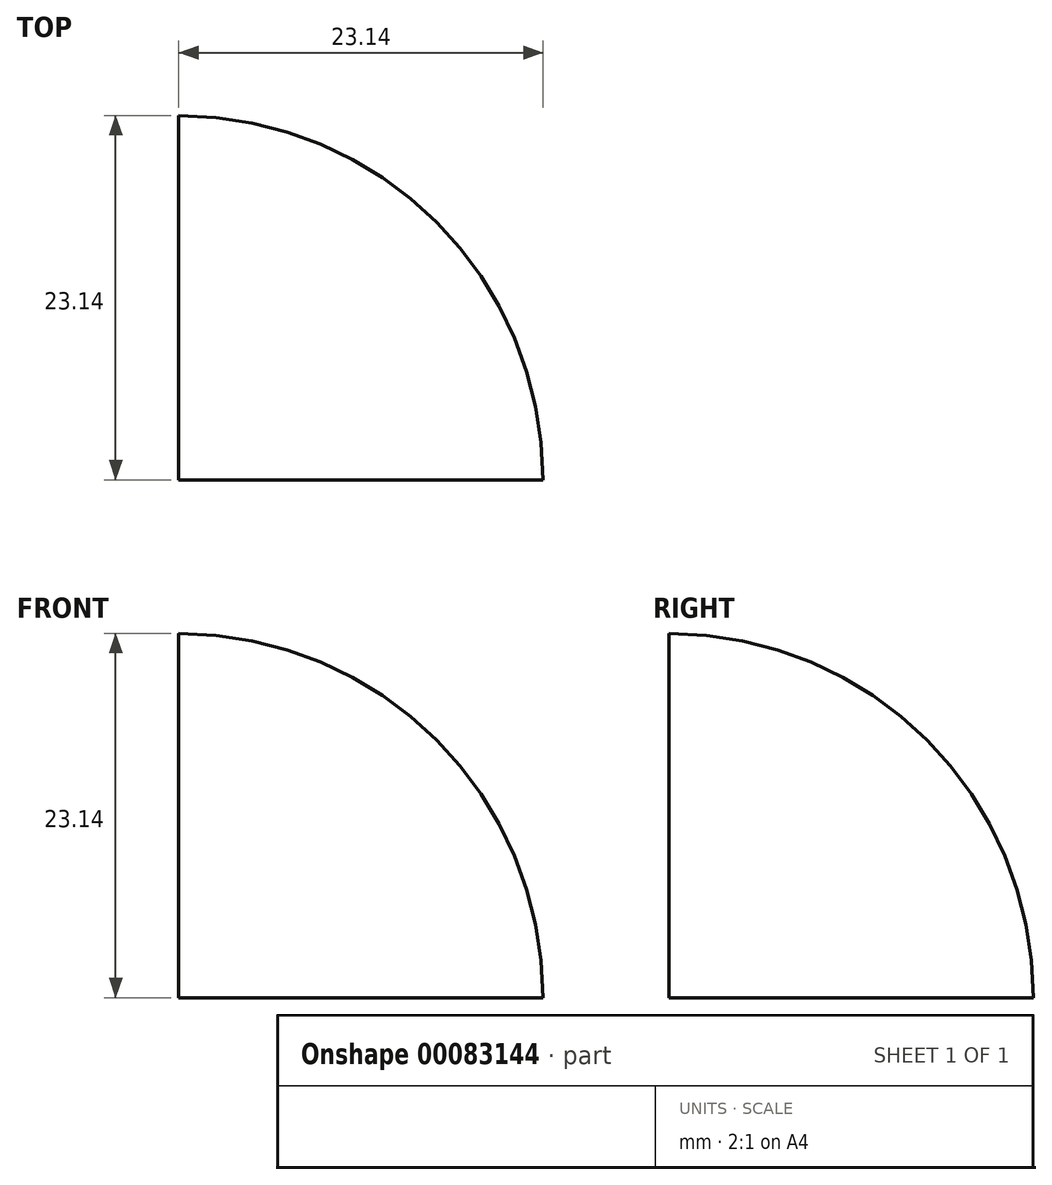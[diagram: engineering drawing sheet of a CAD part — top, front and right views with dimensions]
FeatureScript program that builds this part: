
annotation { "Feature Type Name" : "Feature", "Feature Type Description" : "" }
export const myFeature = defineFeature(function(context is Context, id is Id, definition is map)
    precondition{}
    {
        {
            var Q0;
            Q0=qCreatedBy(makeId("Front.planeOp"),FACE);
            var sketch = newSketch(context, id + "F0", { "sketchPlane" : qUnion([Q0])});
            skPoint(sketch, "E0", {"position": v(0, 0) * mm});
            skPoint(sketch, "E1", {"position": v(35.52, 0) * mm});
            skPoint(sketch, "E2", {"position": v(0, 23.14) * mm});
            skLineSegment(sketch, "E3", {"start": v(0, 0) * mm, "end": v(35.52, 0) * mm});
            skLineSegment(sketch, "E4", {"start": v(0, 0) * mm, "end": v(0, 23.14) * mm});
            skArc(sketch, "E5", {"start": v(0, 23.14) * mm, "mid": v(16.36, 16.36) * mm, "end": v(23.14, 0) * mm});
            skArc(sketch, "E6", {"start": v(0, 27.63) * mm, "mid": v(19.54, 19.54) * mm, "end": v(27.63, 0) * mm});
            skLineSegment(sketch, "E7", {"start": v(0, 23.14) * mm, "end": v(0, 27.63) * mm});
            skLineSegment(sketch, "E8", {"start": v(23.14, 0) * mm, "end": v(27.63, 0) * mm});
            skSolve(sketch);
        }
        {
            var Q0;
            Q0=makeQuery(id+"F0.imprint","IMPRINT",FACE,{"disambiguationData":[TD([[makeQuery(id+"F0.imprint","IMPRINT",EDGE,{"derivedFrom":sQuery(id+"F0.wireOp",EDGE,"E5")}),1.0]])]});
            var Q1;
            Q1=sQuery(id+"F0.wireOp",EDGE,"E4");
            revolve(context, id + "F1", {"entities" : qUnion([Q0]), "axis" : qUnion([Q1]), "revolveType" : RevolveType.ONE_DIRECTION, "angle" : 90 * degree});
        }
    });
